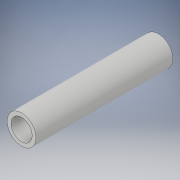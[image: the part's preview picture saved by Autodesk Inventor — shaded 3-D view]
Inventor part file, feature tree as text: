
AUTODESK INVENTOR PART (.ipt)
format: ipt  version: 2019 (Build 230136000, 136)  size: 98,816 bytes
history: native  units: mm
features: extrude x2, sketch x2
ambient origin geometry x8: Origin, YZ Plane, XZ Plane, XY Plane, X Axis, Y Axis, Z Axis, Center Point
bodies: Solid1 (feature_tree)
feature tree (4):
  extrude  "Extrusion1"  Depth=710.5mm TaperAngle=0.0deg
  extrude  "Extrusion2"  Depth=71.05mm TaperAngle=0.0deg
  sketch  "Sketch1"  dims[d0=150.0mm d1=710.5mm d2=0.0mm]
  sketch  "Sketch2"  dims[d3=110.0mm d4=71.05mm d5=0.0mm]
